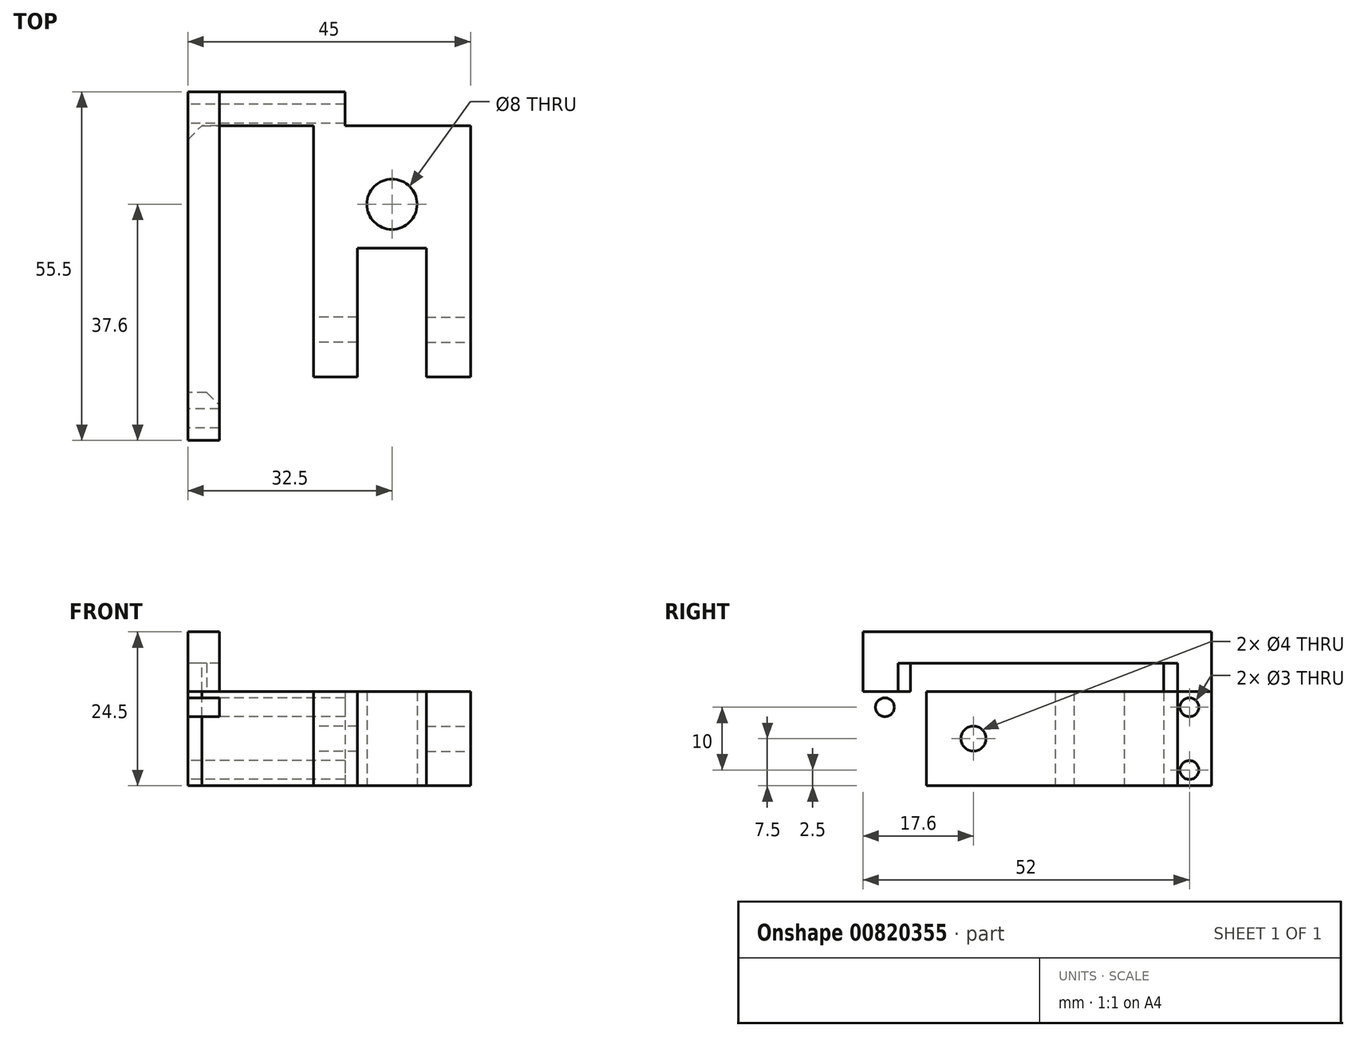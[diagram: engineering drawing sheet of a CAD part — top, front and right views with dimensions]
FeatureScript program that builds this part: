
annotation { "Feature Type Name" : "Feature", "Feature Type Description" : "" }
export const myFeature = defineFeature(function(context is Context, id is Id, definition is map)
    precondition{}
    {
        {
            var Q0;
            Q0=qCreatedBy(makeId("Top.planeOp"),FACE);
            var sketch = newSketch(context, id + "F0", { "sketchPlane" : qUnion([Q0])});
            skLineSegment(sketch, "E0.bottom", {"start": v(12.5, 12.5) * mm, "end": v(-12.5, 12.5) * mm});
            skLineSegment(sketch, "E0.top", {"start": v(12.5, -12.5) * mm, "end": v(-12.5, -12.5) * mm});
            skLineSegment(sketch, "E0.left", {"start": v(12.5, 12.5) * mm, "end": v(12.5, -12.5) * mm});
            skLineSegment(sketch, "E0.right", {"start": v(-12.5, 12.5) * mm, "end": v(-12.5, -12.5) * mm});
            skPoint(sketch, "E0.middle", {"position": v(0, 0) * mm});
            skCircle(sketch, "E1", {"center": v(0, 0) * mm, "radius": 4 * mm});
            skLineSegment(sketch, "E2", {"start": v(-5.5, -12.5) * mm, "end": v(-5.5, -7) * mm});
            skLineSegment(sketch, "E3", {"start": v(-5.5, -7) * mm, "end": v(5.5, -7) * mm});
            skLineSegment(sketch, "E4", {"start": v(5.5, -7) * mm, "end": v(5.5, -12.5) * mm});
            skSolve(sketch);
        }
        {
            var Q0;
            Q0=makeQuery(id+"F0.imprint","IMPRINT",FACE,{"disambiguationData":[TD([[makeQuery(id+"F0.imprint","IMPRINT",EDGE,{"derivedFrom":sQuery(id+"F0.wireOp",EDGE,"E0.bottom")}),1.0]])]});
            extrude(context, id + "F1", {"entities" : qUnion([Q0]), "depth" : 15 * mm, "offsetDistance" : 25 * mm});
        }
        {
            var Q0;
            Q0=makeQuery(id+"F1.opExtrude","SWEPT_FACE",FACE,{"disambiguationData":[OSD([sQuery(id+"F0.wireOp",EDGE,"E0.right")])]});
            cPlane(context, id + "F2", {"entities" : qUnion([Q0]), "cplaneType" : CPlaneType.OFFSET, "offset" : 0 * mm, "width" : 150 * mm, "height" : 150 * mm});
        }
        {
            var Q0;
            Q0=qCreatedBy(id+"F2.planeOp",FACE);
            var sketch = newSketch(context, id + "F3", { "sketchPlane" : qUnion([Q0])});
            skLineSegment(sketch, "E5.0", {"start": v(12.5, 15) * mm, "end": v(12.5, 0) * mm});
            skLineSegment(sketch, "E6", {"start": v(12.5, 15) * mm, "end": v(27.5, 15) * mm});
            skLineSegment(sketch, "E7", {"start": v(27.5, 15) * mm, "end": v(27.5, 0) * mm});
            skLineSegment(sketch, "E8", {"start": v(27.5, 0) * mm, "end": v(12.5, 0) * mm});
            skCircle(sketch, "E9", {"center": v(20, 7.5) * mm, "radius": 2 * mm});
            skSolve(sketch);
        }
        {
            var Q0;
            Q0=makeQuery(id+"F3.imprint","IMPRINT",FACE,{"disambiguationData":[TD([[makeQuery(id+"F3.imprint","IMPRINT",EDGE,{"derivedFrom":sQuery(id+"F3.wireOp",EDGE,"E5.0")}),1.0]])]});
            extrude(context, id + "F4", {"entities" : qUnion([Q0]), "operationType" : NewBodyOperationType.ADD, "oppositeDirection" : true, "depth" : 7 * mm, "offsetDistance" : 25 * mm});
        }
        {
            var Q0;
            Q0=makeQuery(id+"F1.opExtrude","SWEPT_FACE",FACE,{"disambiguationData":[OSD([sQuery(id+"F0.wireOp",EDGE,"E0.left")])]});
            cPlane(context, id + "F5", {"entities" : qUnion([Q0]), "cplaneType" : CPlaneType.OFFSET, "offset" : 0 * mm, "width" : 150 * mm, "height" : 150 * mm});
        }
        {
            var Q0;
            Q0=qCreatedBy(id+"F5.planeOp",FACE);
            var sketch = newSketch(context, id + "F6", { "sketchPlane" : qUnion([Q0])});
            skLineSegment(sketch, "E10.0", {"start": v(-12.5, 15) * mm, "end": v(-12.5, 0) * mm});
            skLineSegment(sketch, "E11.0", {"start": v(-12.5, 15) * mm, "end": v(-27.5, 15) * mm});
            skLineSegment(sketch, "E12.0", {"start": v(-27.5, 15) * mm, "end": v(-27.5, 0) * mm});
            skLineSegment(sketch, "E13.0", {"start": v(-27.5, 0) * mm, "end": v(-12.5, 0) * mm});
            skCircle(sketch, "E14", {"center": v(-20, 7.5) * mm, "radius": 2 * mm});
            skSolve(sketch);
        }
        {
            var Q0;
            Q0=makeQuery(id+"F6.imprint","IMPRINT",FACE,{"disambiguationData":[TD([[makeQuery(id+"F6.imprint","IMPRINT",EDGE,{"derivedFrom":sQuery(id+"F6.wireOp",EDGE,"E10.0")}),-1.0]])]});
            extrude(context, id + "F7", {"entities" : qUnion([Q0]), "operationType" : NewBodyOperationType.ADD, "oppositeDirection" : true, "depth" : 7 * mm, "offsetDistance" : 25 * mm});
        }
        {
            var Q0;
            Q0=qCreatedBy(id+"F2.planeOp",FACE);
            var sketch = newSketch(context, id + "F8", { "sketchPlane" : qUnion([Q0])});
            skLineSegment(sketch, "E15.0", {"start": v(12.5, 15) * mm, "end": v(12.5, 0) * mm});
            skCircle(sketch, "E16.0", {"center": v(20, 7.5) * mm, "radius": 2 * mm});
            skLineSegment(sketch, "E17.0", {"start": v(12.5, 15) * mm, "end": v(27.5, 15) * mm});
            skLineSegment(sketch, "E18.0", {"start": v(27.5, 15) * mm, "end": v(27.5, 0) * mm});
            skLineSegment(sketch, "E19.0", {"start": v(27.5, 0) * mm, "end": v(12.5, 0) * mm});
            skLineSegment(sketch, "E20", {"start": v(30, 17.5) * mm, "end": v(30, -2.5) * mm});
            skLineSegment(sketch, "E21", {"start": v(20, 7.5) * mm, "end": v(30, 7.5) * mm});
            skPoint(sketch, "E21.endSnap0", {"position": v(27.5, 7.5) * mm});
            skLineSegment(sketch, "E22", {"start": v(30, 17.5) * mm, "end": v(-10.3, 17.5) * mm});
            skCircle(sketch, "E23", {"center": v(34.1, 2.5) * mm, "radius": 1.5 * mm});
            skCircle(sketch, "E24.MirrorC", {"center": v(34.1, 12.5) * mm, "radius": 1.5 * mm});
            skLineSegment(sketch, "E25", {"start": v(30, 17.5) * mm, "end": v(37.6, 17.5) * mm});
            skLineSegment(sketch, "E26", {"start": v(37.6, 17.5) * mm, "end": v(37.6, -2.5) * mm});
            skLineSegment(sketch, "E27", {"start": v(37.6, -2.5) * mm, "end": v(30, -2.5) * mm});
            skLineSegment(sketch, "E28", {"start": v(9.85, 17.5) * mm, "end": v(9.85, -2.5) * mm});
            skLineSegment(sketch, "E29.MirrorCS", {"start": v(-10.3, 17.5) * mm, "end": v(-10.3, -2.5) * mm});
            skCircle(sketch, "E30.MirrorC", {"center": v(-14.4, 12.5) * mm, "radius": 1.5 * mm});
            skLineSegment(sketch, "E31.MirrorCS", {"start": v(-10.3, 17.5) * mm, "end": v(-17.9, 17.5) * mm});
            skLineSegment(sketch, "E32.MirrorCS", {"start": v(-17.9, 17.5) * mm, "end": v(-17.9, -2.5) * mm});
            skLineSegment(sketch, "E33.MirrorCS", {"start": v(-17.9, -2.5) * mm, "end": v(-10.3, -2.5) * mm});
            skCircle(sketch, "E34.MirrorC", {"center": v(-14.4, 2.5) * mm, "radius": 1.5 * mm});
            skLineSegment(sketch, "E35", {"start": v(-10.3, -2.5) * mm, "end": v(30, -2.5) * mm});
            skLineSegment(sketch, "E36", {"start": v(27.5, 15) * mm, "end": v(37.6, 15) * mm});
            skLineSegment(sketch, "E37", {"start": v(27.5, 0) * mm, "end": v(37.6, 0) * mm});
            skLineSegment(sketch, "E38.0", {"start": v(-12.5, 15) * mm, "end": v(-12.5, 0) * mm});
            skLineSegment(sketch, "E39", {"start": v(-12.5, 15) * mm, "end": v(-17.9, 15) * mm});
            skLineSegment(sketch, "E40", {"start": v(-12.5, 0) * mm, "end": v(-17.9, 0) * mm});
            skSolve(sketch);
        }
        {
            var Q0;
            Q0=makeQuery(id+"F8.imprint","IMPRINT",FACE,{"disambiguationData":[TD([[makeQuery(id+"F8.imprint","IMPRINT",EDGE,{"derivedFrom":sQuery(id+"F8.wireOp",EDGE,"E30.MirrorC")}),-1.0]])]});
            extrude(context, id + "F9", {"entities" : qUnion([Q0]), "operationType" : NewBodyOperationType.ADD, "oppositeDirection" : true, "depth" : 5 * mm, "offsetDistance" : 25 * mm});
        }
        {
            var Q0;
            Q0=makeQuery(id+"F8.imprint","IMPRINT",FACE,{"disambiguationData":[TD([[makeQuery(id+"F8.imprint","IMPRINT",EDGE,{"derivedFrom":sQuery(id+"F8.wireOp",EDGE,"E30.MirrorC")}),-1.0]])]});
            extrude(context, id + "F10", {"entities" : qUnion([Q0]), "operationType" : NewBodyOperationType.ADD, "depth" : 20 * mm, "offsetDistance" : 25 * mm});
        }
        {
            var Q0;
            Q0=makeQuery(id+"F10.opExtrude","CAP_FACE",FACE,{"disambiguationData":[OSD([sQuery(id+"F8.wireOp",EDGE,"E30.MirrorC"),sQuery(id+"F8.wireOp",EDGE,"E32.MirrorCS"),sQuery(id+"F8.wireOp",EDGE,"E34.MirrorC"),sQuery(id+"F8.wireOp",EDGE,"E38.0"),sQuery(id+"F8.wireOp",EDGE,"E39"),sQuery(id+"F8.wireOp",EDGE,"E40")])],"isStart":false});
            cPlane(context, id + "F11", {"entities" : qUnion([Q0]), "cplaneType" : CPlaneType.OFFSET, "offset" : 0 * mm, "width" : 150 * mm, "height" : 150 * mm});
        }
        {
            var Q0;
            Q0=qCreatedBy(id+"F11.planeOp",FACE);
            var sketch = newSketch(context, id + "F12", { "sketchPlane" : qUnion([Q0])});
            skLineSegment(sketch, "E41.0", {"start": v(30, 17.5) * mm, "end": v(30, -2.5) * mm});
            skLineSegment(sketch, "E42.0", {"start": v(37.6, 17.5) * mm, "end": v(37.6, -2.5) * mm});
            skLineSegment(sketch, "E43.0", {"start": v(27.5, 15) * mm, "end": v(37.6, 15) * mm});
            skLineSegment(sketch, "E44.0", {"start": v(27.5, 0) * mm, "end": v(37.6, 0) * mm});
            skCircle(sketch, "E45.0", {"center": v(34.1, 12.5) * mm, "radius": 1.5 * mm});
            skCircle(sketch, "E46.0", {"center": v(34.1, 2.5) * mm, "radius": 1.5 * mm});
            skLineSegment(sketch, "E47.0", {"start": v(-10.3, 17.5) * mm, "end": v(-17.9, 17.5) * mm});
            skLineSegment(sketch, "E48.0", {"start": v(-17.9, 17.5) * mm, "end": v(-17.9, -2.5) * mm});
            skLineSegment(sketch, "E49.0", {"start": v(30, 17.5) * mm, "end": v(-10.3, 17.5) * mm});
            skLineSegment(sketch, "E50.0", {"start": v(30, 17.5) * mm, "end": v(37.6, 17.5) * mm});
            skLineSegment(sketch, "E51.0", {"start": v(-12.5, 15) * mm, "end": v(-12.5, 0) * mm});
            skLineSegment(sketch, "E52", {"start": v(-12.5, 15) * mm, "end": v(-12.5, 17.5) * mm});
            skLineSegment(sketch, "E53", {"start": v(-17.9, 17.5) * mm, "end": v(-17.9, 24.5) * mm});
            skLineSegment(sketch, "E54", {"start": v(-17.9, 24.5) * mm, "end": v(37.6, 24.5) * mm});
            skLineSegment(sketch, "E55", {"start": v(37.6, 24.5) * mm, "end": v(37.6, 17.5) * mm});
            skLineSegment(sketch, "E56", {"start": v(-12.5, 17.5) * mm, "end": v(-12.5, 19.5) * mm});
            skLineSegment(sketch, "E57", {"start": v(-12.5, 19.5) * mm, "end": v(30, 19.5) * mm});
            skLineSegment(sketch, "E58", {"start": v(30, 19.5) * mm, "end": v(30, 17.5) * mm});
            skLineSegment(sketch, "E59.0", {"start": v(-12.5, 15) * mm, "end": v(-17.9, 15) * mm});
            skLineSegment(sketch, "E60.0", {"start": v(-12.5, 0) * mm, "end": v(-17.9, 0) * mm});
            skLineSegment(sketch, "E61.0", {"start": v(-10.3, 17.5) * mm, "end": v(-10.3, -2.5) * mm});
            skLineSegment(sketch, "E62", {"start": v(-12.5, 15) * mm, "end": v(-10.3, 15) * mm});
            skLineSegment(sketch, "E63", {"start": v(-12.5, 0) * mm, "end": v(-10.3, 0) * mm});
            skLineSegment(sketch, "E64", {"start": v(-10.3, 17.5) * mm, "end": v(-10.3, 19.5) * mm});
            skSolve(sketch);
        }
        {
            var Q0;
            {var subQ3=sQuery(id+"F12.wireOp",EDGE,"E52");Q0=makeQuery(id+"F12.imprint","IMPRINT",FACE,{"disambiguationData":[TD([[makeQuery(id+"F12.imprint","IMPRINT",EDGE,{"derivedFrom":subQ3}),1.0]])]});}
            var Q1;
            Q1=makeQuery(id+"F12.imprint","IMPRINT",FACE,{"disambiguationData":[TD([[makeQuery(id+"F12.imprint","IMPRINT",EDGE,{"derivedFrom":sQuery(id+"F12.wireOp",EDGE,"E50.0")}),1.0]])]});
            var Q2;
            {var subQ0=sQuery(id+"F12.wireOp",EDGE,"E50.0");Q2=makeQuery(id+"F12.imprint","IMPRINT",FACE,{"disambiguationData":[TD([[makeQuery(id+"F12.imprint","IMPRINT",EDGE,{"derivedFrom":subQ0}),-1.0]])]});}
            var Q3;
            Q3=makeQuery(id+"F12.imprint","IMPRINT",FACE,{"disambiguationData":[TD([[makeQuery(id+"F12.imprint","IMPRINT",EDGE,{"derivedFrom":sQuery(id+"F12.wireOp",EDGE,"E45.0")}),1.0]])]});
            extrude(context, id + "F13", {"entities" : qUnion([Q0, Q1, Q2, Q3]), "operationType" : NewBodyOperationType.ADD, "oppositeDirection" : true, "depth" : 5 * mm, "offsetDistance" : 25 * mm});
        }
        {
            var Q0;
            Q0=makeQuery(id+"F12.imprint","IMPRINT",FACE,{"disambiguationData":[TD([[makeQuery(id+"F12.imprint","IMPRINT",EDGE,{"derivedFrom":sQuery(id+"F12.wireOp",EDGE,"E51.0")}),1.0]])]});
            var Q1;
            {var subQ3=sQuery(id+"F12.wireOp",EDGE,"E52");Q1=makeQuery(id+"F12.imprint","IMPRINT",FACE,{"disambiguationData":[TD([[makeQuery(id+"F12.imprint","IMPRINT",EDGE,{"derivedFrom":subQ3}),-1.0]])]});}
            var Q2;
            {var subQ2=sQuery(id+"F12.wireOp",EDGE,"E56");Q2=makeQuery(id+"F12.imprint","IMPRINT",FACE,{"disambiguationData":[TD([[makeQuery(id+"F12.imprint","IMPRINT",EDGE,{"derivedFrom":subQ2}),-1.0]])]});}
            extrude(context, id + "F14", {"entities" : qUnion([Q0, Q1, Q2]), "operationType" : NewBodyOperationType.ADD, "oppositeDirection" : true, "depth" : 3 * mm, "offsetDistance" : 25 * mm});
        }
        {
            var Q0;
            Q0=makeQuery(id+"F14.opExtrude","CAP_EDGE",EDGE,{"disambiguationData":[OSD([sQuery(id+"F12.wireOp",EDGE,"E61.0"),sQuery(id+"F12.wireOp",EDGE,"E64")])],"isStart":false});
            chamfer(context, id + "F15", {"entities" : qUnion([Q0]), "width" : 3 * mm, "tangentPropagation" : true});
        }
        {
            var Q0;
            Q0=makeQuery(id+"F13.opExtrude","CAP_EDGE",EDGE,{"disambiguationData":[OSD([sQuery(id+"F12.wireOp",EDGE,"E41.0"),sQuery(id+"F12.wireOp",EDGE,"E58")])],"isStart":false});
            chamfer(context, id + "F16", {"entities" : qUnion([Q0]), "width" : 2 * mm, "tangentPropagation" : true});
        }
    });
